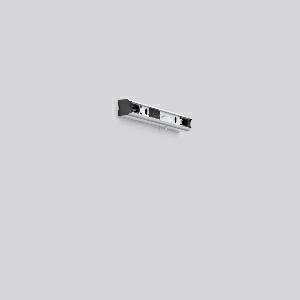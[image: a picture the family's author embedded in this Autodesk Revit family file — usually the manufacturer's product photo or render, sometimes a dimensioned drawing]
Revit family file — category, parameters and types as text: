
# Revit family: alu-stableuchten_41531_004_31e0
name_source: partatom
category: Lighting Fixtures
units: mm (PartAtom-declared; Revit-internal decimal feet)

## family parameters
Cut with Voids When Loaded = No
Host = Face
Light Source = No
Part Type = Normal
Room Calculation Point = No
Round Connector Dimension = Use Diameter
Shared = No

## types (1)
- ALU-Stableuchten (1 x LED L S14S, 1000 lm, 16 W, 2700)
    Apparent Load = 16 VA
    CIE Flux Codes = 34 61 82 75 81
    Color Rendering = 80
    Color Temperature = 2700
    Default Elevation = 1800 mm
    Description = Series: Aluminium striplights
Aluminium striplight for linear lamps. Base: extruded anodised aluminium profile. End caps: plastic. With push button switch. Lamp contacts disconnection during lamp replacement. Light source must be ordered separately. 
Colour: anodised aluminium
Length: 300 mm
Width: 35 mm
Height: 58 mm
Lamp: L-DE
Number of lamps: 1
Wattage: 35 W
Socket: S14s
System power: 30 W
Rated luminous flux: 1100 lm
Luminous efficiency: 37 lm/W
Control gear: Converter not necessary
Protection class: I
Type of protection: IP 40
    Height = 58 mm
    Lamp = 1 x LED L S14S
    Lamp Light Flux = 1000 lm
    Lamp Power = 16 W
    Lamp count = 1
    Length = 300 mm
    Lifetime = 25000 h
    Luminous efficacy = 51 lm/W
    Manufacturer = RZB
    ModVariant = No
    Model = 41531.004
    Mounting Place = Ceiling, Wall
    Mounting Type = Surface mounted
    Number of Poles = 1
    OnlyDefault = Yes
    Power Factor = 1
    Product Name = ALU-Stableuchten
    Product group = Surface mounted ceiling and wall luminaires
    ProductGroupID = 305
    Protection Class = Protection class I
    Protection Degree = IP 40
    RLX_Detail_Level = 1
    RLX_Emergency_Light_Flux = 0 lm
    RLX_Emergency_Type = 0
    RLX_Emergency_Type_DB = No
    RlxData = <blob elided: 11849 chars, md5=3b2754aa>
    Socket = S14s
    Standby Power = 0 W
    System Light Flux = 813 lm
    System Power = 16 W
    Type Comments = Product without accessories
    Type Image = 41531.004.jpg
    URL = http://relux.com
    VarID = ---
    Voltage = 230 V
    Voltage Range = 220-240 V
    Weight = 0.00 kg
    Width = 35 mm

## geometry (parser evidence)
native form markers: Sweep x11
no freeform markers — native parametric forms only
